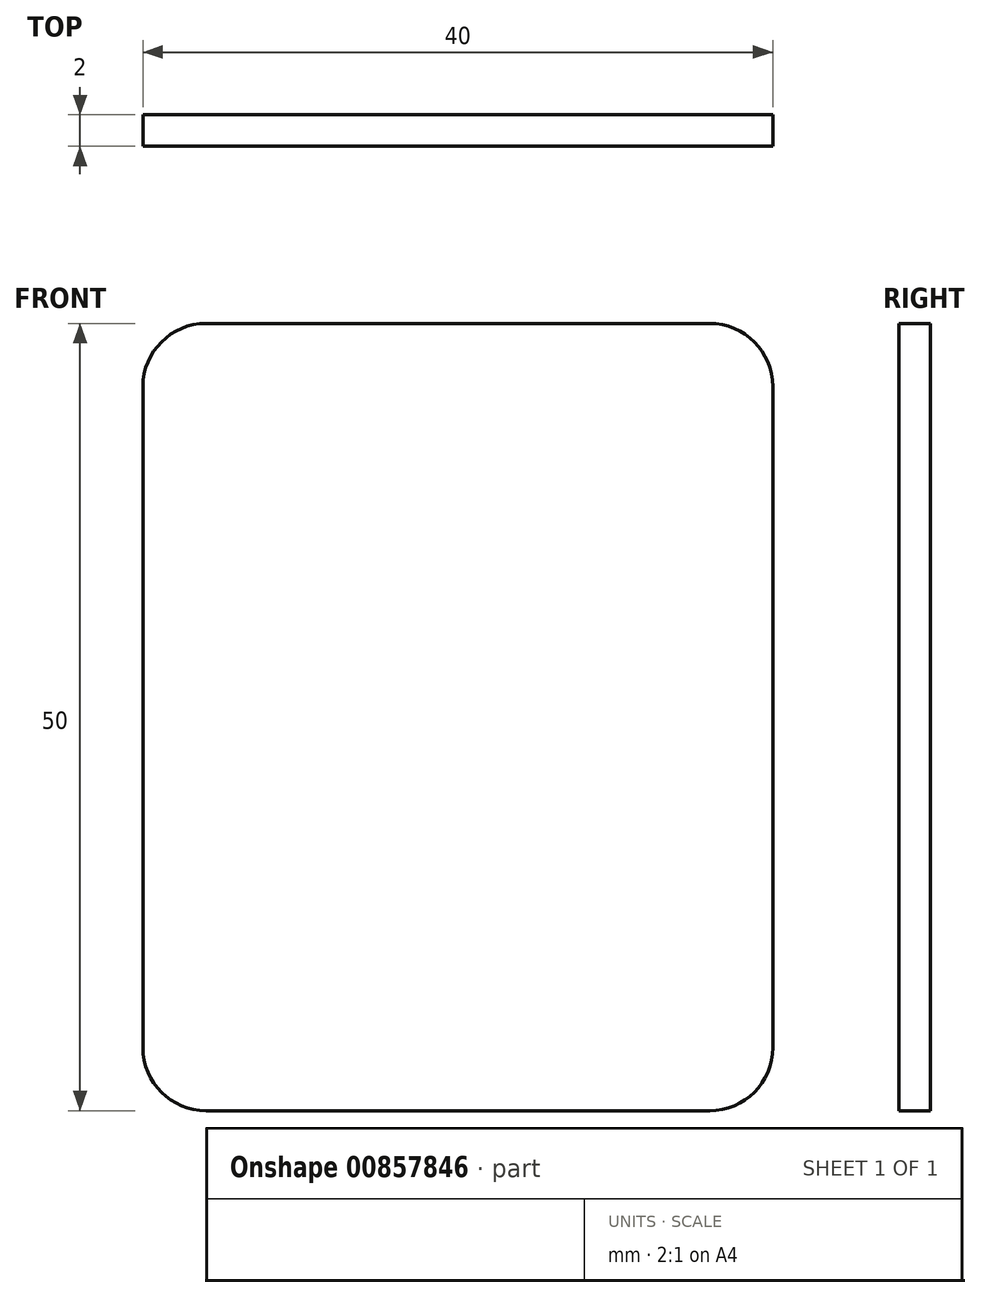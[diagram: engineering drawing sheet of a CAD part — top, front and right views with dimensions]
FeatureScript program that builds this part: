
annotation { "Feature Type Name" : "Feature", "Feature Type Description" : "" }
export const myFeature = defineFeature(function(context is Context, id is Id, definition is map)
    precondition{}
    {
        {
            var Q0;
            Q0=qCreatedBy(makeId("Front.planeOp"),FACE);
            var sketch = newSketch(context, id + "F0", { "sketchPlane" : qUnion([Q0])});
            skLineSegment(sketch, "E0.bottom", {"start": v(4, 0) * mm, "end": v(36, 0) * mm});
            skLineSegment(sketch, "E0.top", {"start": v(4, -50) * mm, "end": v(36, -50) * mm});
            skLineSegment(sketch, "E0.left", {"start": v(0, -4) * mm, "end": v(0, -46) * mm});
            skLineSegment(sketch, "E0.right", {"start": v(40, -4) * mm, "end": v(40, -46) * mm});
            skPoint(sketch, "E1.visualSharp", {"position": v(0, 0) * mm});
            skArc(sketch, "E1.filletArc", {"start": v(4, 0) * mm, "mid": v(1.17, -1.17) * mm, "end": v(0, -4) * mm});
            skPoint(sketch, "E2.visualSharp", {"position": v(0, -50) * mm});
            skArc(sketch, "E2.filletArc", {"start": v(0, -46) * mm, "mid": v(1.17, -48.83) * mm, "end": v(4, -50) * mm});
            skPoint(sketch, "E3.visualSharp", {"position": v(40, -50) * mm});
            skArc(sketch, "E3.filletArc", {"start": v(36, -50) * mm, "mid": v(38.83, -48.83) * mm, "end": v(40, -46) * mm});
            skPoint(sketch, "E4.visualSharp", {"position": v(40, 0) * mm});
            skArc(sketch, "E4.filletArc", {"start": v(40, -4) * mm, "mid": v(38.83, -1.17) * mm, "end": v(36, 0) * mm});
            skSolve(sketch);
        }
        {
            var Q0;
            Q0=makeQuery(id+"F0.imprint","IMPRINT",FACE,{"disambiguationData":[TD([[makeQuery(id+"F0.imprint","IMPRINT",EDGE,{"derivedFrom":sQuery(id+"F0.wireOp",EDGE,"E0.bottom")}),-1.0]])]});
            extrude(context, id + "F1", {"entities" : qUnion([Q0]), "depth" : 2 * mm, "offsetDistance" : 25 * mm});
        }
    });
